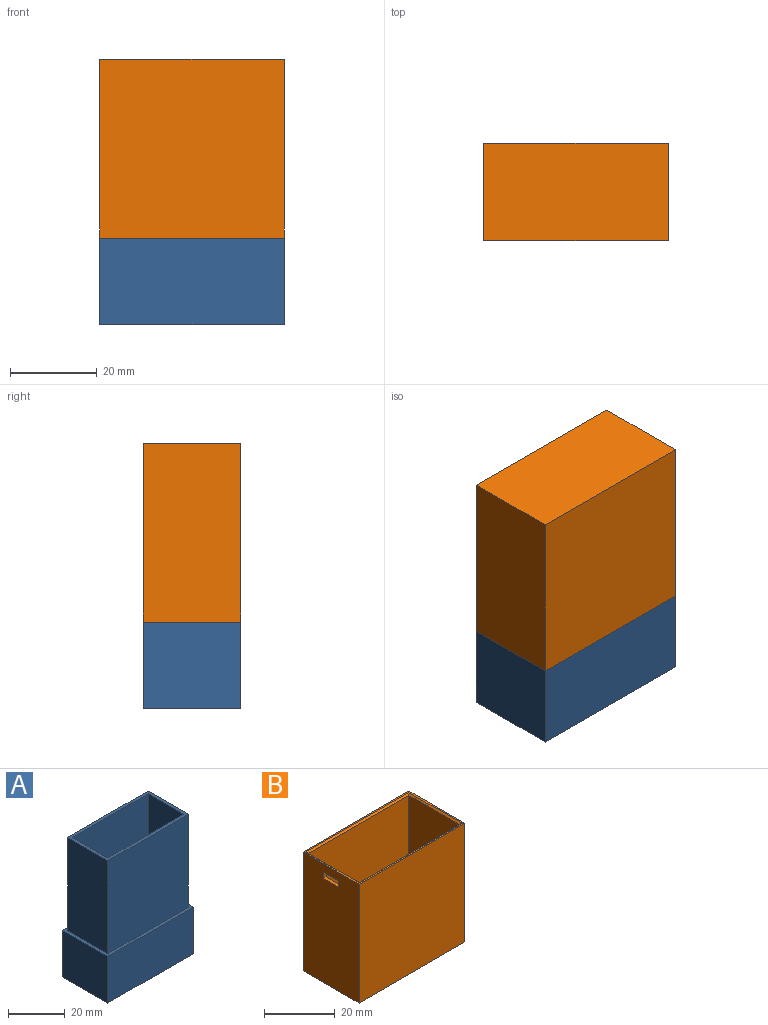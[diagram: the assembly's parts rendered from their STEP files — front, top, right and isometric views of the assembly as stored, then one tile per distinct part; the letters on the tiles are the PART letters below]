
ASSEMBLY  parts=2 mates=1
PART A: 21 faces, bbox 42.4x22.4x60 mm
  f0: plane 2x0.94mm, normal (0,-1,0), area 1.2mm2, adj f1,f18,f19,f20
  f1: plane 40x20mm, normal (1,0,0), area 788mm2, adj f0,f2,f4,f5,f15,f17,f18,f19
  f2: plane 40x40mm, normal (0,1,0), area 1600mm2, adj f1,f3,f5,f15
  f3: plane 40x20mm, normal (-1,0,0), area 800mm2, adj f2,f4,f5,f15
  f4: plane 40x40mm, normal (0,-1,0), area 1600mm2, adj f1,f3,f5,f15
  f5: plane 40x20mm, normal (0,0,1), area 138.2mm2, adj f1,f2,f3,f4,f6,f7,f8,f9
  f6: plane 58.8x17.6mm, normal (-1,0,0), area 1034.9mm2, adj f5,f7,f9,f10
  f7: plane 58.8x37.6mm, normal (0,-1,0), area 2210.9mm2, adj f5,f6,f8,f10
  f8: plane 58.8x17.6mm, normal (1,0,0), area 1034.9mm2, adj f5,f7,f9,f10
  f9: plane 58.8x37.6mm, normal (0,1,0), area 2210.9mm2, adj f5,f6,f8,f10
  f10: plane 37.6x17.6mm, normal (0,0,1), area 661.8mm2, adj f6,f7,f8,f9
  f11: plane 22.4x20mm, normal (1,0,0), area 448mm2, adj f12,f14,f15,f16
  f12: plane 42.4x20mm, normal (0,-1,0), area 848mm2, adj f11,f13,f15,f16
  f13: plane 22.4x20mm, normal (-1,0,0), area 448mm2, adj f12,f14,f15,f16
  f14: plane 42.4x20mm, normal (0,1,0), area 848mm2, adj f11,f13,f15,f16
  f15: plane 42.4x22.4mm, normal (0,0,1), area 149.8mm2, adj f1,f2,f3,f4,f11,f12,f13,f14
  f16: plane 42.4x22.4mm, normal (0,0,-1), area 949.8mm2, adj f11,f12,f13,f14
  f17: plane 2x0.94mm, normal (0,1,0), area 1.2mm2, adj f1,f18,f19,f20
  f18: plane 6x0.44mm, normal (0,0,-1), area 2.6mm2, adj f0,f1,f17,f20
  f19: plane 6x1.21mm, normal (0.82,0,0.57), area 8.9mm2, adj f0,f1,f17,f20
  f20: cylinder r=0.5mm len=6mm, axis (0,1,0), area 6.5mm2, adj f0,f17,f18,f19
PART B: 20 faces, bbox 42.4x22.4x41.2 mm
  f0: plane 39.5x20.3mm, normal (1,0,0), area 785.1mm2, adj f4,f5,f10,f11,f12,f13,f15,f18
  f1: plane 41.2x22.4mm, normal (-1,0,0), area 909.2mm2, adj f2,f7,f8,f9,f11,f12,f13,f14
  f2: plane 42.4x22.4mm, normal (0,0,-1), area 949.8mm2, adj f1,f6,f7,f8
  f3: plane 39.5x20.3mm, normal (-1,0,0), area 801.8mm2, adj f4,f5,f10,f17
  f4: plane 40.3x39.5mm, normal (0,-1,0), area 1591.8mm2, adj f0,f3,f10,f19
  f5: plane 40.3x39.5mm, normal (0,1,0), area 1591.8mm2, adj f0,f3,f10,f16
  f6: plane 41.2x22.4mm, normal (1,0,0), area 922.9mm2, adj f2,f7,f8,f9
  f7: plane 42.4x41.2mm, normal (0,-1,0), area 1746.9mm2, adj f1,f2,f6,f9
  f8: plane 42.4x41.2mm, normal (0,1,0), area 1746.9mm2, adj f1,f2,f6,f9
  f9: plane 42.4x22.4mm, normal (0,0,1), area 70.1mm2, adj f1,f6,f7,f8,f16,f17,f18,f19
  f10: plane 40.3x20.3mm, normal (0,0,1), area 818.1mm2, adj f0,f3,f4,f5
  f11: plane 2.7x1.05mm, normal (0,-1,0), area 2.4mm2, adj f0,f1,f12,f14,f15
  f12: plane 6.2x1.05mm, normal (0,0,1), area 6.5mm2, adj f0,f1,f11,f13
  f13: plane 2.7x1.05mm, normal (0,1,0), area 2.4mm2, adj f0,f1,f12,f14,f15
  f14: plane 6.2x0.55mm, normal (0,0,-1), area 3.4mm2, adj f1,f11,f13,f15
  f15: plane 6.2x0.5mm, normal (0.71,0,-0.71), area 4.4mm2, adj f0,f11,f13,f14
  f16: plane 41.3x0.5mm, normal (0,0.71,0.71), area 28.8mm2, adj f5,f9,f17,f18
  f17: plane 21.3x0.5mm, normal (-0.71,0,0.71), area 14.7mm2, adj f3,f9,f16,f19
  f18: plane 21.3x0.5mm, normal (0.71,0,0.71), area 14.7mm2, adj f0,f9,f16,f19
  f19: plane 41.3x0.5mm, normal (0,-0.71,0.71), area 28.8mm2, adj f4,f9,f17,f18
PLACE A at identity
PLACE B rot(axis=(0,1,0),180deg) t=(1.45,0,61.2)mm
MATE slider B.f10 <-> A.f5  axis (0,0,-1) through (0,0,60)mm
